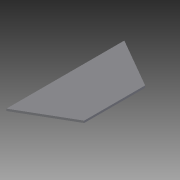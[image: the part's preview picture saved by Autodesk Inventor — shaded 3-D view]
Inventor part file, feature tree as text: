
AUTODESK INVENTOR PART (.ipt)
format: ipt  version: 2015 (Build 190159000, 159)  size: 71,168 bytes
history: native  units: in
note: dims shown in document units (in); Inventor stores cm internally (conversion verified against a paired STEP export)
features: extrude x1, sketch x1
ambient origin geometry x8: Origin, YZ Plane, XZ Plane, XY Plane, X Axis, Y Axis, Z Axis, Center Point
bodies: Solid1 (feature_tree)
feature tree (2):
  extrude  "Extrusion1"  TaperAngle=30.0deg  [1 undecoded]
  sketch  "Sketch1"  dims[d0=120.0deg d1=30.0deg d3=7.0in d4=0.25in d5=0.0in d6=5.0in]
note: 1 required parameter value undecoded (feature->parameter linkage not recoverable at this tier; creation-order binding heuristic only, values carry confidence <= 0.55)
